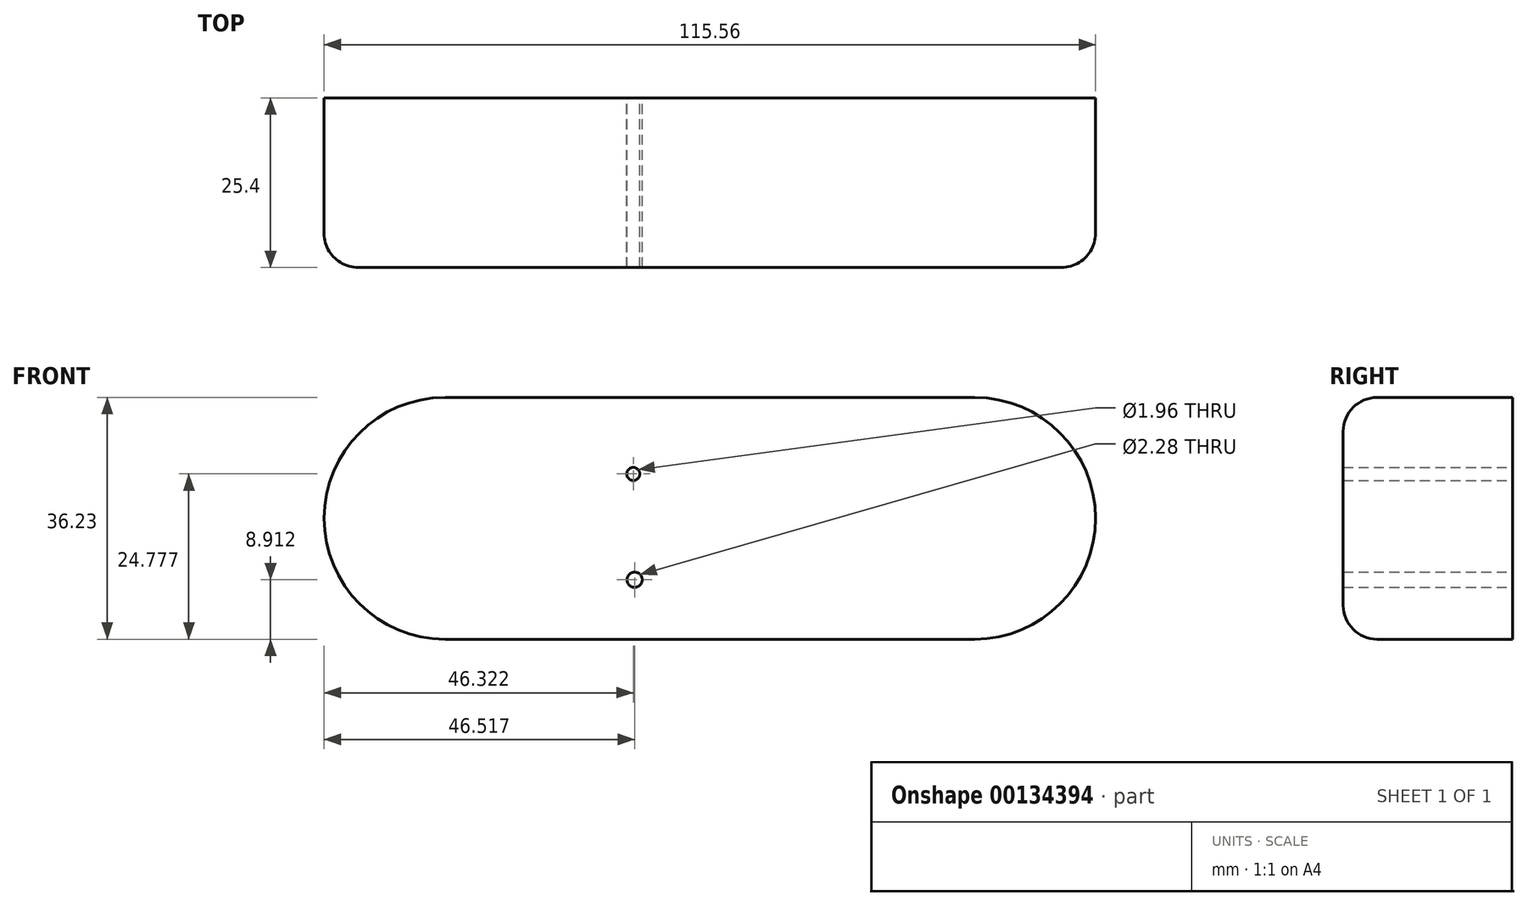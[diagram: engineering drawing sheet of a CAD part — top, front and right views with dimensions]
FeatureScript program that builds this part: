
annotation { "Feature Type Name" : "Feature", "Feature Type Description" : "" }
export const myFeature = defineFeature(function(context is Context, id is Id, definition is map)
    precondition{}
    {
        {
            var Q0;
            Q0=qCreatedBy(makeId("Front.planeOp"),FACE);
            var sketch = newSketch(context, id + "F0", { "sketchPlane" : qUnion([Q0])});
            skLineSegment(sketch, "E0", {"start": v(-42.01, 36.23) * mm, "end": v(37.31, 36.23) * mm});
            skArc(sketch, "E1", {"start": v(-42.01, 36.23) * mm, "mid": v(-60.13, 18.12) * mm, "end": v(-42.01, 0) * mm});
            skLineSegment(sketch, "E2", {"start": v(-42.01, 0) * mm, "end": v(37.31, 0) * mm});
            skArc(sketch, "E3", {"start": v(37.31, 0) * mm, "mid": v(55.43, 18.12) * mm, "end": v(37.31, 36.23) * mm});
            skLineSegment(sketch, "E4", {"start": v(-25.95, 27.32) * mm, "end": v(-25.95, 6.37) * mm});
            skCircle(sketch, "E5", {"center": v(-13.8, 24.78) * mm, "radius": 0.98 * mm});
            skCircle(sketch, "E6", {"center": v(-13.61, 8.91) * mm, "radius": 1.14 * mm});
            skCircle(sketch, "E7", {"center": v(8.13, 17.33) * mm, "radius": 12.35 * mm});
            skCircle(sketch, "E8", {"center": v(37.31, 18.12) * mm, "radius": 12.17 * mm});
            skSolve(sketch);
        }
        {
            var Q0;
            Q0=makeQuery(id+"F0.imprint","IMPRINT",FACE,{"disambiguationData":[TD([[makeQuery(id+"F0.imprint","IMPRINT",EDGE,{"derivedFrom":sQuery(id+"F0.wireOp",EDGE,"E0")}),-1.0]])]});
            var Q1;
            Q1=makeQuery(id+"F0.imprint","IMPRINT",FACE,{"disambiguationData":[TD([[makeQuery(id+"F0.imprint","IMPRINT",EDGE,{"derivedFrom":sQuery(id+"F0.wireOp",EDGE,"E7")}),1.0]])]});
            var Q2;
            Q2=makeQuery(id+"F0.imprint","IMPRINT",FACE,{"disambiguationData":[TD([[makeQuery(id+"F0.imprint","IMPRINT",EDGE,{"derivedFrom":sQuery(id+"F0.wireOp",EDGE,"E8")}),1.0]])]});
            extrude(context, id + "F1", {"entities" : qUnion([Q0, Q1, Q2]), "depth" : 25.4 * mm});
        }
        {
            var Q0;
            Q0=makeQuery(id+"F1.opExtrude","CAP_EDGE",EDGE,{"disambiguationData":[OSD([sQuery(id+"F0.wireOp",EDGE,"E1")])],"isStart":false});
            var Q1;
            Q1=makeQuery(id+"F1.opExtrude","CAP_EDGE",EDGE,{"disambiguationData":[OSD([sQuery(id+"F0.wireOp",EDGE,"E0")])],"isStart":false});
            var Q2;
            Q2=makeQuery(id+"F1.opExtrude","CAP_EDGE",EDGE,{"disambiguationData":[OSD([sQuery(id+"F0.wireOp",EDGE,"E2")])],"isStart":false});
            var Q3;
            Q3=makeQuery(id+"F1.opExtrude","CAP_EDGE",EDGE,{"disambiguationData":[OSD([sQuery(id+"F0.wireOp",EDGE,"E3")])],"isStart":false});
            fillet(context, id + "F2", {"entities" : qUnion([Q0, Q1, Q2, Q3]), "radius" : 5.08 * mm, "tangentPropagation" : true, "allowEdgeOverflow" : false});
        }
    });
